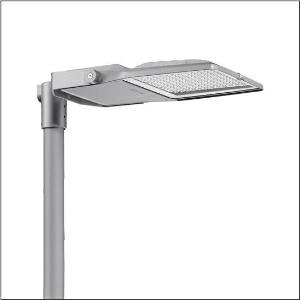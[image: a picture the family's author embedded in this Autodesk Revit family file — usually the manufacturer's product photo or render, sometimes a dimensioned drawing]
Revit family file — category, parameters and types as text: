
# Revit family: floodlight_fl_21_midi___pl52_5xa7785e2d3a_ba97
name_source: partatom
category: Lighting Fixtures
units: mm (PartAtom-declared; Revit-internal decimal feet)

## family parameters
Cut with Voids When Loaded = No
Host = Face
Light Source = No
Part Type = Normal
Room Calculation Point = No
Round Connector Dimension = Use Diameter
Shared = No

## types (1)
- --- (1 x LED, 26940 lm, 212.4 W, 3000K)
    Apparent Load = 212 VA
    CIE Flux Codes = 26 60 98 100 100
    Color Rendering = 70
    Color Temperature = 3000K
    Default Elevation = 1800 mm
    Description = Floodlight FL 21 midi, floodlight, primary light control with lens, of PMMA, primary optical cover: protective disc, of toughened safety glass, transparent, light distribution: PL52, light emission: direct distribution, installation type: surface-mounted, LED, High Power LED, rated luminous flux: 26.940lm, luminous efficacy: 127lm/W, light colour: 730, colour temperature: 3000K, control gear: ECG Smart Interface, control: flexible luminous flux parameterisation, time-dependent luminous flux control, constant luminous flux control, overheat protection, presetting dimming logarithmic, with terminal, 6-pole, mains connection: 220..240V, AC, 50/60Hz, start of lifetime: 212W, end of service life: 231W, reduction: 95W, luminaire housing, of diecast aluminium, powder-coated, Siteco® metallic grey (DB 702S), sealing non-destructively replaceable, please order mast flange separately, mast bracket, of steel, galvanised, powder-coated, Siteco® metallic grey (DB 702S), Smart Interface above, protection rating (complete): IP66, insulation class (complete): insulation class II (safety insulation), certification: CE, protection symbol: D, impact resistance: IK08, permissible operating ambient temperature: -20..+40°C, permissible operating ambient temperature for outdoor applications: -40..+50°C, standard: DIN EN 12944, LABS conformity tested according to VDMA 24364:2018-05, packaging unit: 1 piece

Light Distribution: PL52
    Height = 76 mm
    Lamp = 1 x LED
    Lamp Light Flux = 26940 lm
    Lamp Power = 212.4 W
    Lamp count = 1
    Length = 657 mm
    Luminous efficacy = 127 lm/W
    Manufacturer = Siteco
    ModVariant = No
    Model = 5XA7785E2D3A
    Number of Poles = 1
    OnlyDefault = Yes
    Power Factor = 1
    Product Name = Floodlight FL 21 midi | PL52
    Product group = floodlight | pylon annexe
    ProductGroupID = 6200
    Protection Class = Protection class II
    Protection Degree = IP 66
    RLX_Detail_Level = 1
    RLX_Emergency_Light_Flux = 0 lm
    RLX_Emergency_Type = 0
    RLX_Emergency_Type_DB = No
    RlxData = <blob elided: 153549 chars, md5=2f282303>
    Socket = socket
    Standby Power = 0 W
    System Light Flux = 26940 lm
    System Power = 212 W
    Type Comments = factory setting: luminous flux: 100 % | dim-lin: 254 | 710 mA
    Type Image = l_1007123.jpg
    URL = http://relux.com
    VarID = @adj_128815
    Voltage = 0 V
    Weight = 0.00 kg
    Width = 442 mm

## geometry (parser evidence)
native form markers: Blend x4, Sweep x12
no freeform markers — native parametric forms only
